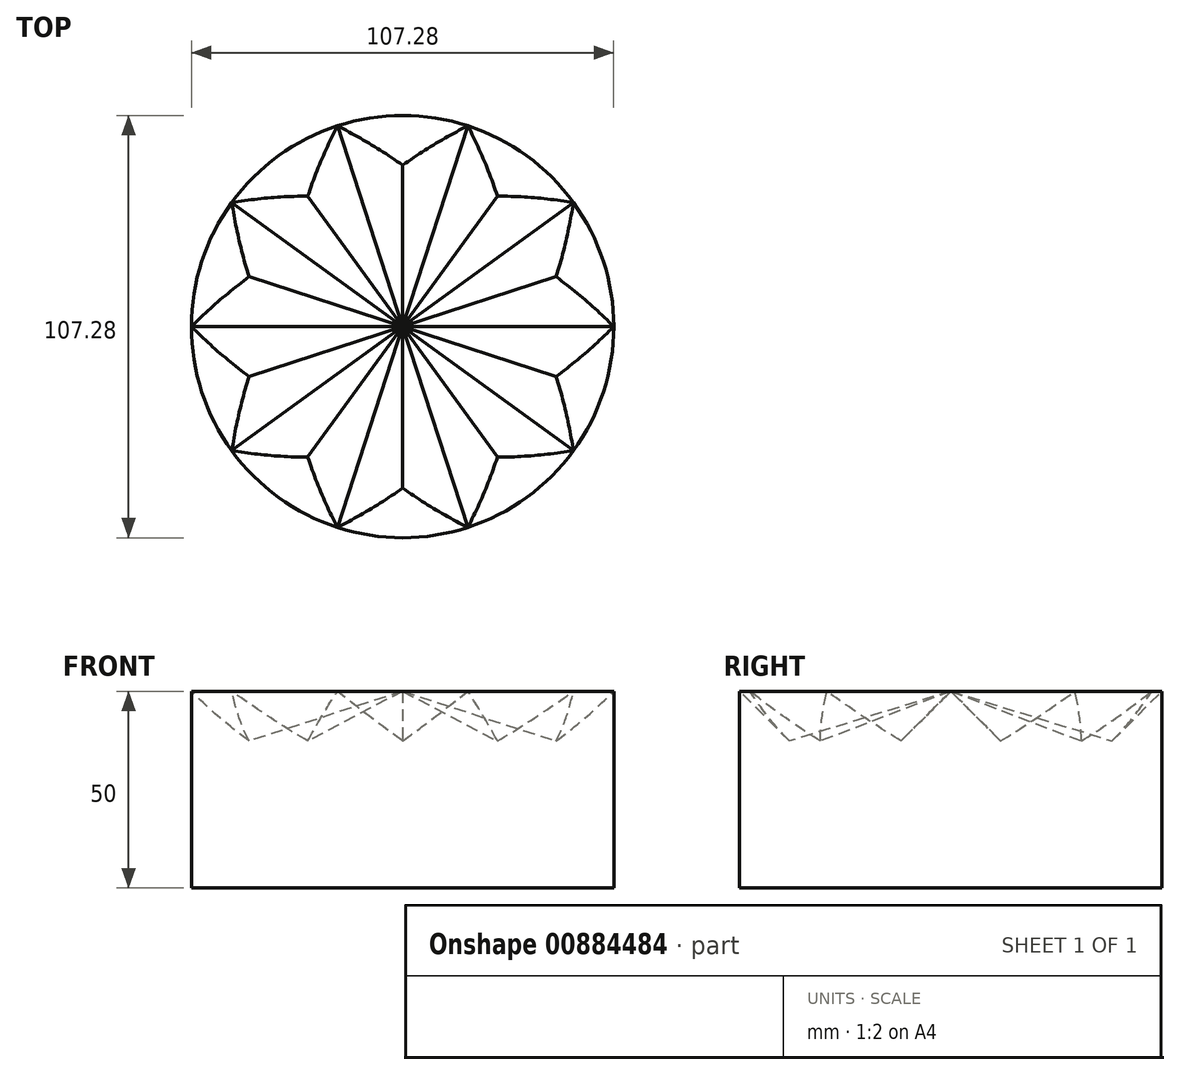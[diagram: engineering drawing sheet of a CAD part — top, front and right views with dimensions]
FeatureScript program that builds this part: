
annotation { "Feature Type Name" : "Feature", "Feature Type Description" : "" }
export const myFeature = defineFeature(function(context is Context, id is Id, definition is map)
    precondition{}
    {
        {
            var Q0;
            Q0=qCreatedBy(makeId("Top.planeOp"),FACE);
            var sketch = newSketch(context, id + "F0", { "sketchPlane" : qUnion([Q0])});
            skCircle(sketch, "E0", {"center": v(0, 0) * mm, "radius": 53.64 * mm});
            skLineSegment(sketch, "E1", {"start": v(0, 0) * mm, "end": v(53.64, 0) * mm});
            skLineSegment(sketch, "E2.1.0", {"start": v(0, 0) * mm, "end": v(43.4, 31.53) * mm});
            skLineSegment(sketch, "E2.2.0", {"start": v(0, 0) * mm, "end": v(16.58, 51.02) * mm});
            skLineSegment(sketch, "E2.3.0", {"start": v(0, 0) * mm, "end": v(-16.58, 51.02) * mm});
            skLineSegment(sketch, "E2.4.0", {"start": v(0, 0) * mm, "end": v(-43.4, 31.53) * mm});
            skLineSegment(sketch, "E2.5.0", {"start": v(0, 0) * mm, "end": v(-53.64, 0) * mm});
            skLineSegment(sketch, "E2.6.0", {"start": v(0, 0) * mm, "end": v(-43.4, -31.53) * mm});
            skLineSegment(sketch, "E2.7.0", {"start": v(0, 0) * mm, "end": v(-16.58, -51.02) * mm});
            skLineSegment(sketch, "E2.8.0", {"start": v(0, 0) * mm, "end": v(16.58, -51.02) * mm});
            skLineSegment(sketch, "E2.9.0", {"start": v(0, 0) * mm, "end": v(43.4, -31.53) * mm});
            skSolve(sketch);
        }
        {
            var Q0;
            Q0=qCreatedBy(makeId("Top.planeOp"),FACE);
            var sketch = newSketch(context, id + "F1", { "sketchPlane" : qUnion([Q0])});
            skCircle(sketch, "E3", {"center": v(0, 0) * mm, "radius": 53.64 * mm});
            skLineSegment(sketch, "E4", {"start": v(0, 0) * mm, "end": v(53.64, 0) * mm});
            skLineSegment(sketch, "E5.1.0", {"start": v(0, 0) * mm, "end": v(43.4, 31.53) * mm});
            skLineSegment(sketch, "E5.2.0", {"start": v(0, 0) * mm, "end": v(16.58, 51.02) * mm});
            skLineSegment(sketch, "E5.3.0", {"start": v(0, 0) * mm, "end": v(-16.58, 51.02) * mm});
            skLineSegment(sketch, "E5.4.0", {"start": v(0, 0) * mm, "end": v(-43.4, 31.53) * mm});
            skLineSegment(sketch, "E5.5.0", {"start": v(0, 0) * mm, "end": v(-53.64, 0) * mm});
            skLineSegment(sketch, "E5.6.0", {"start": v(0, 0) * mm, "end": v(-43.4, -31.53) * mm});
            skLineSegment(sketch, "E5.7.0", {"start": v(0, 0) * mm, "end": v(-16.58, -51.02) * mm});
            skLineSegment(sketch, "E5.8.0", {"start": v(0, 0) * mm, "end": v(16.58, -51.02) * mm});
            skLineSegment(sketch, "E5.9.0", {"start": v(0, 0) * mm, "end": v(43.4, -31.53) * mm});
            skSolve(sketch);
        }
        {
            var Q0;
            Q0 = qSketchRegion(id + "F0", true);
            extrude(context, id + "F2", {"entities" : qUnion([Q0]), "oppositeDirection" : true, "depth" : 50 * mm, "offsetDistance" : 25 * mm});
        }
        {
            var Q0;
            {var subQ0=sQuery(id+"F0.wireOp",EDGE,"E2.8.0");Q0=makeQuery(id+"F0.imprint","IMPRINT",FACE,{"disambiguationData":[TD([[makeQuery(id+"F0.imprint","IMPRINT",EDGE,{"derivedFrom":subQ0}),1.0]])]});}
            var Q1;
            {var subQ0=sQuery(id+"F0.wireOp",EDGE,"E1");Q1=makeQuery(id+"F0.imprint","IMPRINT",FACE,{"disambiguationData":[TD([[makeQuery(id+"F0.imprint","IMPRINT",EDGE,{"derivedFrom":subQ0}),1.0]])]});}
            var Q2;
            {var subQ0=sQuery(id+"F0.wireOp",EDGE,"E2.2.0");Q2=makeQuery(id+"F0.imprint","IMPRINT",FACE,{"disambiguationData":[TD([[makeQuery(id+"F0.imprint","IMPRINT",EDGE,{"derivedFrom":subQ0}),1.0]])]});}
            var Q3;
            {var subQ0=sQuery(id+"F0.wireOp",EDGE,"E2.4.0");Q3=makeQuery(id+"F0.imprint","IMPRINT",FACE,{"disambiguationData":[TD([[makeQuery(id+"F0.imprint","IMPRINT",EDGE,{"derivedFrom":subQ0}),1.0]])]});}
            var Q4;
            {var subQ0=sQuery(id+"F0.wireOp",EDGE,"E2.6.0");Q4=makeQuery(id+"F0.imprint","IMPRINT",FACE,{"disambiguationData":[TD([[makeQuery(id+"F0.imprint","IMPRINT",EDGE,{"derivedFrom":subQ0}),1.0]])]});}
            extrude(context, id + "F3", {"entities" : qUnion([Q0, Q1, Q2, Q3, Q4]), "operationType" : NewBodyOperationType.REMOVE, "oppositeDirection" : true, "depth" : 25 * mm, "offsetDistance" : 25 * mm, "hasDraft" : true, "draftAngle" : 45 * degree, "draftPullDirection" : true});
        }
        {
            var Q0;
            {var subQ0=sQuery(id+"F1.wireOp",EDGE,"E5.5.0");Q0=makeQuery(id+"F1.imprint","IMPRINT",FACE,{"disambiguationData":[TD([[makeQuery(id+"F1.imprint","IMPRINT",EDGE,{"derivedFrom":subQ0}),1.0]])]});}
            var Q1;
            {var subQ0=sQuery(id+"F1.wireOp",EDGE,"E5.7.0");Q1=makeQuery(id+"F1.imprint","IMPRINT",FACE,{"disambiguationData":[TD([[makeQuery(id+"F1.imprint","IMPRINT",EDGE,{"derivedFrom":subQ0}),1.0]])]});}
            var Q2;
            {var subQ0=sQuery(id+"F1.wireOp",EDGE,"E4");Q2=makeQuery(id+"F1.imprint","IMPRINT",FACE,{"disambiguationData":[TD([[makeQuery(id+"F1.imprint","IMPRINT",EDGE,{"derivedFrom":subQ0}),-1.0]])]});}
            var Q3;
            {var subQ0=sQuery(id+"F1.wireOp",EDGE,"E5.1.0");Q3=makeQuery(id+"F1.imprint","IMPRINT",FACE,{"disambiguationData":[TD([[makeQuery(id+"F1.imprint","IMPRINT",EDGE,{"derivedFrom":subQ0}),1.0]])]});}
            var Q4;
            {var subQ0=sQuery(id+"F1.wireOp",EDGE,"E5.3.0");Q4=makeQuery(id+"F1.imprint","IMPRINT",FACE,{"disambiguationData":[TD([[makeQuery(id+"F1.imprint","IMPRINT",EDGE,{"derivedFrom":subQ0}),1.0]])]});}
            extrude(context, id + "F4", {"entities" : qUnion([Q0, Q1, Q2, Q3, Q4]), "operationType" : NewBodyOperationType.REMOVE, "oppositeDirection" : true, "depth" : 25 * mm, "offsetDistance" : 25 * mm, "hasDraft" : true, "draftAngle" : 45 * degree, "draftPullDirection" : true});
        }
    });
